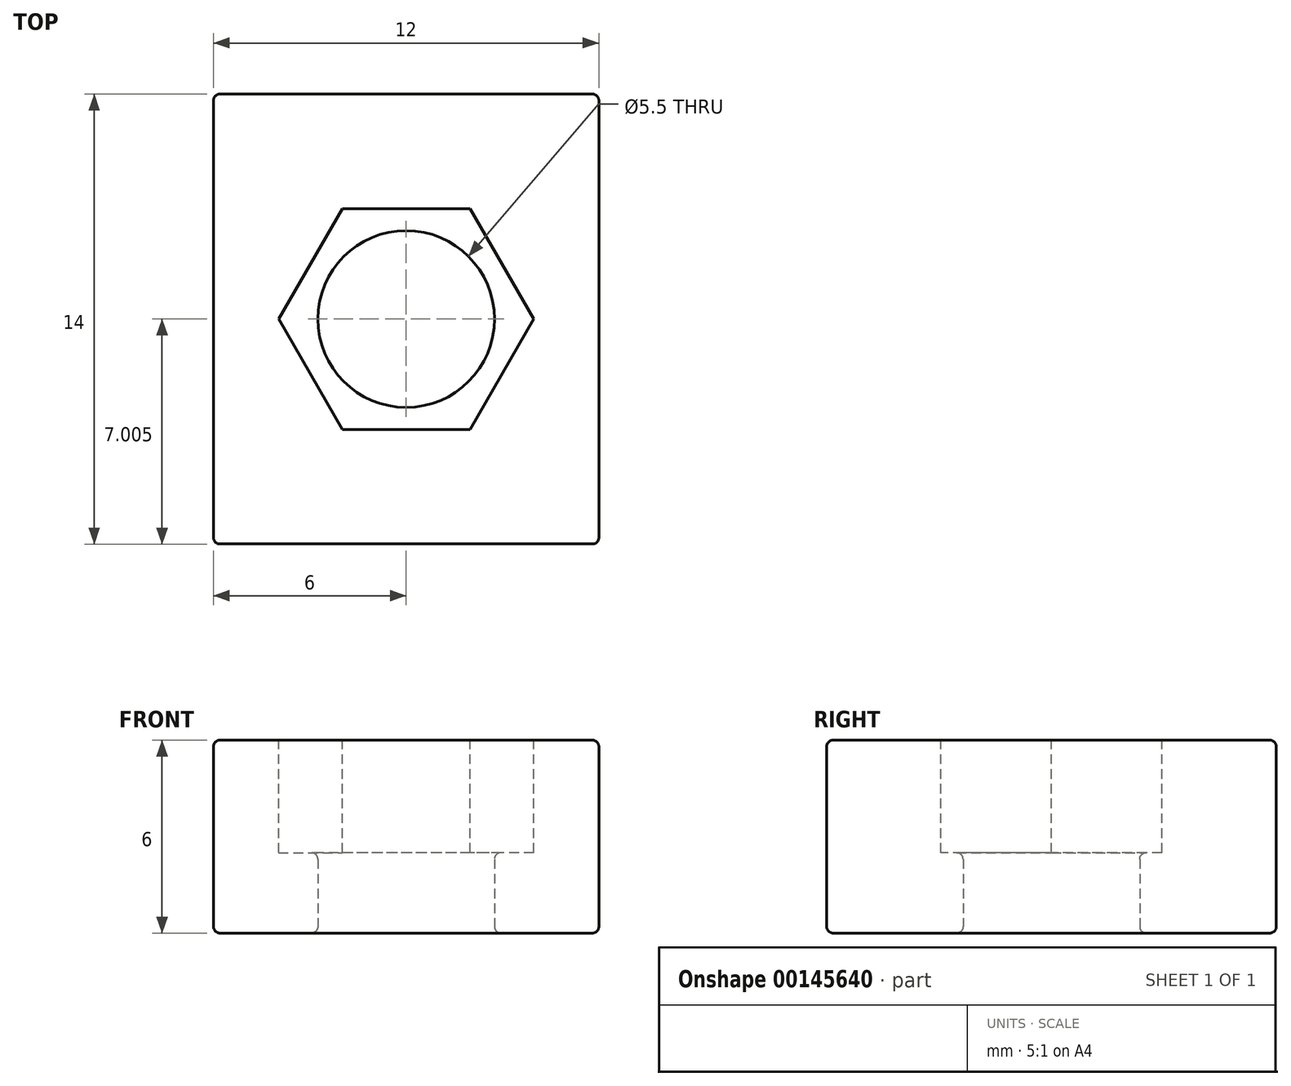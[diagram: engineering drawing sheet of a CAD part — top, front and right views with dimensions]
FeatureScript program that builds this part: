
annotation { "Feature Type Name" : "Feature", "Feature Type Description" : "" }
export const myFeature = defineFeature(function(context is Context, id is Id, definition is map)
    precondition{}
    {
        {
            var Q0;
            Q0=qCreatedBy(makeId("Top.planeOp"),FACE);
            var sketch = newSketch(context, id + "F4", { "sketchPlane" : qUnion([Q0])});
            skLineSegment(sketch, "E0.bottom", {"start": v(0, 0) * mm, "end": v(0, 0) * mm});
            skLineSegment(sketch, "E0.top", {"start": v(0, 0) * mm, "end": v(0, 0) * mm});
            skLineSegment(sketch, "E0.left", {"start": v(0, 0) * mm, "end": v(0, 0) * mm});
            skLineSegment(sketch, "E0.right", {"start": v(0, 0) * mm, "end": v(0, 0) * mm});
            skPoint(sketch, "E0.middle", {"position": v(0, 0) * mm});
            skLineSegment(sketch, "E1.bottom", {"start": v(0, 9.01) * mm, "end": v(12, 9.01) * mm});
            skLineSegment(sketch, "E1.top", {"start": v(0, -4.99) * mm, "end": v(12, -4.99) * mm});
            skLineSegment(sketch, "E1.left", {"start": v(0, 9.01) * mm, "end": v(0, -4.99) * mm});
            skLineSegment(sketch, "E1.right", {"start": v(12, 9.01) * mm, "end": v(12, -4.99) * mm});
            skPoint(sketch, "E1.middle", {"position": v(6, 2.01) * mm});
            skCircle(sketch, "E2", {"center": v(6, 2.01) * mm, "radius": 2.75 * mm});
            skSolve(sketch);
        }
        {
            var Q0;
            Q0=makeQuery(id+"F4.imprint","IMPRINT",FACE,{"disambiguationData":[TD([[makeQuery(id+"F4.imprint","IMPRINT",EDGE,{"derivedFrom":sQuery(id+"F4.wireOp",EDGE,"E1.bottom")}),-1.0]])]});
            extrude(context, id + "F0", {"entities" : qUnion([Q0]), "depth" : 6 * mm});
        }
        {
            var Q0;
            Q0=makeQuery(id+"F0.opExtrude","CAP_FACE",FACE,{"disambiguationData":[OSD([sQuery(id+"F4.wireOp",EDGE,"E1.bottom"),sQuery(id+"F4.wireOp",EDGE,"E1.top"),sQuery(id+"F4.wireOp",EDGE,"E1.left"),sQuery(id+"F4.wireOp",EDGE,"E1.right"),sQuery(id+"F4.wireOp",EDGE,"E2")])],"isStart":false});
            var sketch = newSketch(context, id + "F1", { "sketchPlane" : qUnion([Q0])});
            skCircle(sketch, "E3.cCircle", {"center": v(6, 2.01) * mm, "radius": 3.44 * mm, "construction": true});
            skPoint(sketch, "E3.cCircle.perimeterSnap0", {"position": v(6, -4.99) * mm});
            skLineSegment(sketch, "E3.0", {"start": v(7.99, -1.42) * mm, "end": v(4.01, -1.42) * mm});
            skLineSegment(sketch, "E3.1", {"start": v(4.01, -1.42) * mm, "end": v(2.03, 2.01) * mm});
            skLineSegment(sketch, "E3.2", {"start": v(2.03, 2.01) * mm, "end": v(4.01, 5.45) * mm});
            skLineSegment(sketch, "E3.3", {"start": v(4.01, 5.45) * mm, "end": v(7.98, 5.45) * mm});
            skLineSegment(sketch, "E3.4", {"start": v(7.98, 5.45) * mm, "end": v(9.97, 2.01) * mm});
            skLineSegment(sketch, "E3.5", {"start": v(9.97, 2.01) * mm, "end": v(7.98, -1.42) * mm});
            skPoint(sketch, "E3.0.midPoint", {"position": v(6, -1.42) * mm});
            skPoint(sketch, "E3.0.midPoint.positionSnap0", {"position": v(6, -4.99) * mm});
            skSolve(sketch);
        }
        {
            var Q0;
            Q0 = qSketchRegion(id + "F1", true);
            extrude(context, id + "F5", {"entities" : qUnion([Q0]), "operationType" : NewBodyOperationType.REMOVE, "oppositeDirection" : true, "depth" : 3.5 * mm});
        }
        {
            var Q0;
            Q0=makeQuery(id+"F0.opExtrude","CAP_EDGE",EDGE,{"disambiguationData":[OSD([sQuery(id+"F4.wireOp",EDGE,"E1.top")])],"isStart":false});
            var Q1;
            Q1=makeQuery(id+"F0.opExtrude","CAP_EDGE",EDGE,{"disambiguationData":[OSD([sQuery(id+"F4.wireOp",EDGE,"E1.left")])],"isStart":false});
            var Q2;
            Q2=makeQuery(id+"F0.opExtrude","CAP_EDGE",EDGE,{"disambiguationData":[OSD([sQuery(id+"F4.wireOp",EDGE,"E1.bottom")])],"isStart":false});
            var Q3;
            Q3=makeQuery(id+"F0.opExtrude","CAP_EDGE",EDGE,{"disambiguationData":[OSD([sQuery(id+"F4.wireOp",EDGE,"E1.right")])],"isStart":false});
            var Q4;
            Q4=makeQuery(id+"F5.boolean.opBoolean","COPY",EDGE,{"derivedFrom":makeQuery(id+"F5.opExtrude","CAP_EDGE",EDGE,{"disambiguationData":[OSD([sQuery(id+"F1.wireOp",EDGE,"E3.3")])],"isStart":true})});
            var Q5;
            Q5=makeQuery(id+"F5.boolean.opBoolean","COPY",EDGE,{"derivedFrom":makeQuery(id+"F5.opExtrude","CAP_EDGE",EDGE,{"disambiguationData":[OSD([sQuery(id+"F1.wireOp",EDGE,"E3.4")])],"isStart":true})});
            var Q6;
            Q6=makeQuery(id+"F5.boolean.opBoolean","COPY",EDGE,{"derivedFrom":makeQuery(id+"F5.opExtrude","CAP_EDGE",EDGE,{"disambiguationData":[OSD([sQuery(id+"F1.wireOp",EDGE,"E3.5")])],"isStart":true})});
            var Q7;
            Q7=makeQuery(id+"F5.boolean.opBoolean","COPY",EDGE,{"derivedFrom":makeQuery(id+"F5.opExtrude","CAP_EDGE",EDGE,{"disambiguationData":[OSD([sQuery(id+"F1.wireOp",EDGE,"E3.0")])],"isStart":true})});
            var Q8;
            Q8=makeQuery(id+"F5.boolean.opBoolean","COPY",EDGE,{"derivedFrom":makeQuery(id+"F5.opExtrude","CAP_EDGE",EDGE,{"disambiguationData":[OSD([sQuery(id+"F1.wireOp",EDGE,"E3.1")])],"isStart":true})});
            var Q9;
            Q9=makeQuery(id+"F5.boolean.opBoolean","COPY",EDGE,{"derivedFrom":makeQuery(id+"F5.opExtrude","CAP_EDGE",EDGE,{"disambiguationData":[OSD([sQuery(id+"F1.wireOp",EDGE,"E3.2")])],"isStart":true})});
            var Q10;
            Q10=makeQuery(id+"F5.boolean.opBoolean","INTERSECT",EDGE,{"derivedFrom":[makeQuery(id+"F0.opExtrude","SWEPT_FACE",FACE,{"disambiguationData":[OSD([sQuery(id+"F4.wireOp",EDGE,"E2")])]}),makeQuery(id+"F5.opExtrude","CAP_FACE",FACE,{"disambiguationData":[OSD([sQuery(id+"F1.wireOp",EDGE,"E3.0"),sQuery(id+"F1.wireOp",EDGE,"E3.1"),sQuery(id+"F1.wireOp",EDGE,"E3.2"),sQuery(id+"F1.wireOp",EDGE,"E3.3"),sQuery(id+"F1.wireOp",EDGE,"E3.4"),sQuery(id+"F1.wireOp",EDGE,"E3.5")])],"isStart":false})]});
            var Q11;
            Q11=makeQuery(id+"F0.opExtrude","SWEPT_EDGE",EDGE,{"disambiguationData":[OSD([sQuery(id+"F4.wireOp",EDGE,"E1.top"),sQuery(id+"F4.wireOp",EDGE,"E1.right")])]});
            var Q12;
            Q12=makeQuery(id+"F0.opExtrude","SWEPT_EDGE",EDGE,{"disambiguationData":[OSD([sQuery(id+"F4.wireOp",EDGE,"E1.bottom"),sQuery(id+"F4.wireOp",EDGE,"E1.right")])]});
            var Q13;
            Q13=makeQuery(id+"F0.opExtrude","CAP_EDGE",EDGE,{"disambiguationData":[OSD([sQuery(id+"F4.wireOp",EDGE,"E1.right")])],"isStart":true});
            var Q14;
            Q14=makeQuery(id+"F0.opExtrude","CAP_EDGE",EDGE,{"disambiguationData":[OSD([sQuery(id+"F4.wireOp",EDGE,"E1.top")])],"isStart":true});
            var Q15;
            Q15=makeQuery(id+"F0.opExtrude","SWEPT_EDGE",EDGE,{"disambiguationData":[OSD([sQuery(id+"F4.wireOp",EDGE,"E1.top"),sQuery(id+"F4.wireOp",EDGE,"E1.left")])]});
            var Q16;
            Q16=makeQuery(id+"F0.opExtrude","CAP_EDGE",EDGE,{"disambiguationData":[OSD([sQuery(id+"F4.wireOp",EDGE,"E2")])],"isStart":true});
            var Q17;
            Q17=makeQuery(id+"F0.opExtrude","CAP_EDGE",EDGE,{"disambiguationData":[OSD([sQuery(id+"F4.wireOp",EDGE,"E1.bottom")])],"isStart":true});
            var Q18;
            Q18=makeQuery(id+"F0.opExtrude","SWEPT_EDGE",EDGE,{"disambiguationData":[OSD([sQuery(id+"F4.wireOp",EDGE,"E1.bottom"),sQuery(id+"F4.wireOp",EDGE,"E1.left")])]});
            fillet(context, id + "F2", {"entities" : qUnion([Q0, Q1, Q2, Q3, Q4, Q5, Q6, Q7, Q8, Q9, Q10, Q11, Q12, Q13, Q14, Q15, Q16, Q17, Q18]), "radius" : .2 * mm, "tangentPropagation" : true, "allowEdgeOverflow" : false});
        }
        {
            var Q0;
            Q0=makeQuery(id+"F0.opExtrude","CAP_EDGE",EDGE,{"disambiguationData":[OSD([sQuery(id+"F4.wireOp",EDGE,"E1.left")])],"isStart":true});
            fillet(context, id + "F3", {"entities" : qUnion([Q0]), "radius" : .2 * mm, "tangentPropagation" : true, "allowEdgeOverflow" : false});
        }
    });
